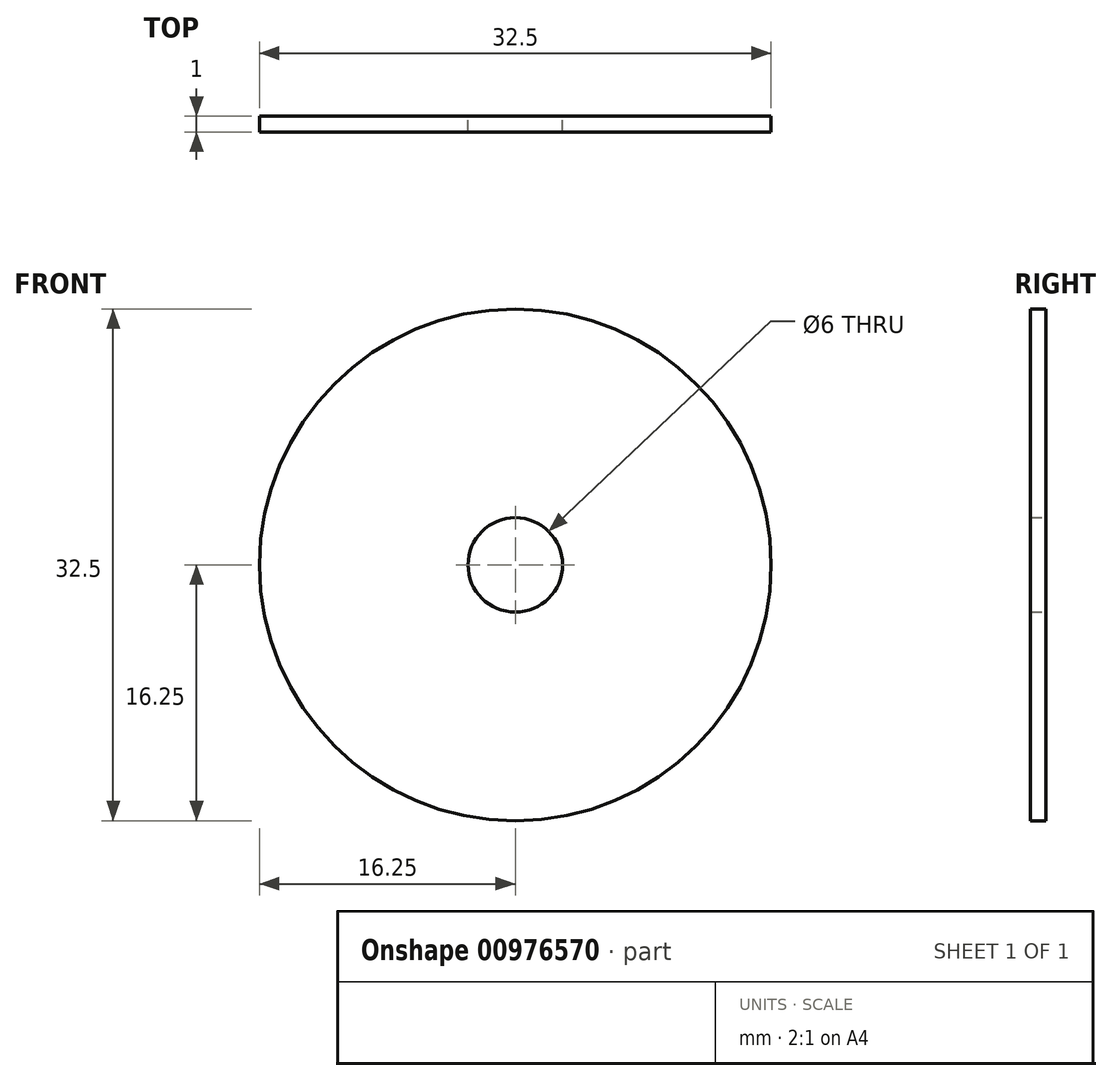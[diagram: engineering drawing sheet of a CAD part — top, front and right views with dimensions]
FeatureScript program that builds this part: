
annotation { "Feature Type Name" : "Feature", "Feature Type Description" : "" }
export const myFeature = defineFeature(function(context is Context, id is Id, definition is map)
    precondition{}
    {
        {
            var Q0;
            Q0=qCreatedBy(makeId("Front.planeOp"),FACE);
            var sketch = newSketch(context, id + "F0", { "sketchPlane" : qUnion([Q0])});
            skCircle(sketch, "E0", {"center": v(0, 0) * mm, "radius": 16.25 * mm});
            skCircle(sketch, "E1", {"center": v(0, 0) * mm, "radius": 3 * mm});
            skSolve(sketch);
        }
        {
            var Q0;
            Q0=makeQuery(id+"F0.imprint","IMPRINT",FACE,{"disambiguationData":[TD([[makeQuery(id+"F0.imprint","IMPRINT",EDGE,{"derivedFrom":sQuery(id+"F0.wireOp",EDGE,"E0")}),1.0]])]});
            extrude(context, id + "F1", {"entities" : qUnion([Q0]), "depth" : 1 * mm, "offsetDistance" : 25 * mm});
        }
    });
